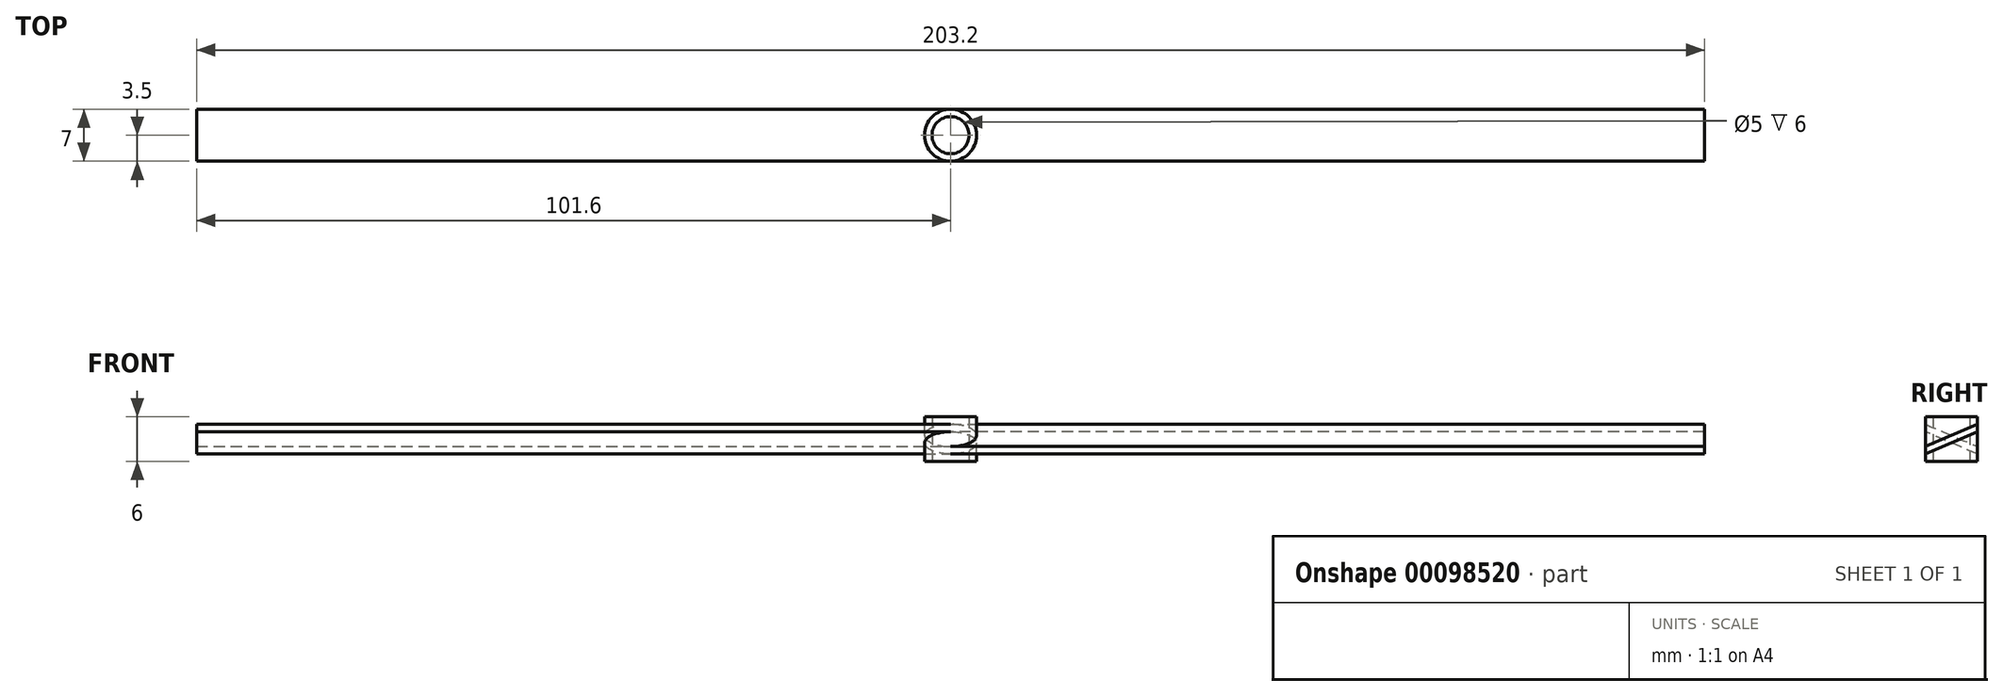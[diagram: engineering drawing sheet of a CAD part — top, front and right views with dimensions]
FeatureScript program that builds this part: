
annotation { "Feature Type Name" : "Feature", "Feature Type Description" : "" }
export const myFeature = defineFeature(function(context is Context, id is Id, definition is map)
    precondition{}
    {
        {
            var Q0;
            Q0=qCreatedBy(makeId("Top.planeOp"),FACE);
            var sketch = newSketch(context, id + "F0", { "sketchPlane" : qUnion([Q0])});
            skCircle(sketch, "E0", {"center": v(0, 0) * mm, "radius": 2.5 * mm});
            skLineSegment(sketch, "E1", {"start": v(0, 0) * mm, "end": v(2.5, 0) * mm});
            skLineSegment(sketch, "E2", {"start": v(0, 0) * mm, "end": v(101.6, 0) * mm});
            skLineSegment(sketch, "E3", {"start": v(0, 0) * mm, "end": v(-101.6, 0) * mm});
            skCircle(sketch, "E4", {"center": v(0, 0) * mm, "radius": 3.5 * mm});
            skLineSegment(sketch, "E5", {"start": v(0, 0) * mm, "end": v(0, 3.5) * mm});
            skLineSegment(sketch, "E6", {"start": v(0, 3.5) * mm, "end": v(0, -3.5) * mm});
            skLineSegment(sketch, "E7", {"start": v(0, 3.5) * mm, "end": v(-101.6, 3.5) * mm});
            skLineSegment(sketch, "E8", {"start": v(0, -3.5) * mm, "end": v(-101.6, -3.5) * mm});
            skLineSegment(sketch, "E9", {"start": v(-101.6, -3.5) * mm, "end": v(-101.6, 3.5) * mm});
            skLineSegment(sketch, "E10", {"start": v(0, 3.5) * mm, "end": v(101.6, 3.5) * mm});
            skLineSegment(sketch, "E11", {"start": v(0, -3.5) * mm, "end": v(101.6, -3.5) * mm});
            skLineSegment(sketch, "E12", {"start": v(101.6, -3.5) * mm, "end": v(101.6, 3.5) * mm});
            skSolve(sketch);
        }
        {
            var Q0;
            Q0 = qSketchRegion(id + "F0", true);
            extrude(context, id + "F1", {"entities" : qUnion([Q0]), "depth" : 4 * mm});
        }
        {
            var Q0;
            Q0=makeQuery(id+"F1.opExtrude","CAP_FACE",FACE,{"disambiguationData":[OSD([sQuery(id+"F0.wireOp",EDGE,"E0"),sQuery(id+"F0.wireOp",EDGE,"E7"),sQuery(id+"F0.wireOp",EDGE,"E8"),sQuery(id+"F0.wireOp",EDGE,"E9"),sQuery(id+"F0.wireOp",EDGE,"E10"),sQuery(id+"F0.wireOp",EDGE,"E11"),sQuery(id+"F0.wireOp",EDGE,"E12")])],"isStart":false});
            var sketch = newSketch(context, id + "F2", { "sketchPlane" : qUnion([Q0])});
            skCircle(sketch, "E13", {"center": v(0, 0) * mm, "radius": 3.5 * mm});
            skLineSegment(sketch, "E14", {"start": v(0, 0) * mm, "end": v(3.5, 0) * mm});
            skLineSegment(sketch, "E15", {"start": v(3.5, 0) * mm, "end": v(-3.5, 0) * mm});
            skLineSegment(sketch, "E16", {"start": v(-3.5, 0) * mm, "end": v(-3.5, 3.5) * mm});
            skLineSegment(sketch, "E17", {"start": v(-3.5, 3.5) * mm, "end": v(-3.5, -3.5) * mm});
            skLineSegment(sketch, "E18", {"start": v(3.5, 0) * mm, "end": v(3.5, 3.5) * mm});
            skLineSegment(sketch, "E19", {"start": v(3.5, 3.5) * mm, "end": v(3.5, -3.5) * mm});
            skSolve(sketch);
        }
        {
            var Q0;
            {var subQ0=sQuery(id+"F2.wireOp",EDGE,"E17");var subQ1=sQuery(id+"F2.wireOp",EDGE,"E13");var subQ2=makeQuery(id+"F2.imprint","INTERSECT",VERTEX,{"derivedFrom":[subQ1,sQuery(id+"F2.wireOp",EDGE,"E15"),subQ0]});Q0=makeQuery(id+"F2.imprint","IMPRINT",FACE,{"disambiguationData":[TD([[makeQuery(id+"F2.imprint","IMPRINT",EDGE,{"disambiguationData":[TD([[subQ2,1.0]])],"derivedFrom":subQ1}),-1.0]])]});}
            var Q1;
            {var subQ0=sQuery(id+"F2.wireOp",EDGE,"E19");var subQ1=sQuery(id+"F2.wireOp",EDGE,"E13");var subQ2=makeQuery(id+"F2.imprint","INTERSECT",VERTEX,{"derivedFrom":[subQ1,sQuery(id+"F2.wireOp",EDGE,"E15"),subQ0]});Q1=makeQuery(id+"F2.imprint","IMPRINT",FACE,{"disambiguationData":[TD([[makeQuery(id+"F2.imprint","IMPRINT",EDGE,{"disambiguationData":[TD([[subQ2,-1.0]])],"derivedFrom":subQ1}),-1.0]])]});}
            var Q2;
            {var subQ0=sQuery(id+"F2.wireOp",EDGE,"E19");var subQ1=sQuery(id+"F2.wireOp",EDGE,"E13");var subQ2=makeQuery(id+"F2.imprint","INTERSECT",VERTEX,{"derivedFrom":[subQ1,sQuery(id+"F2.wireOp",EDGE,"E15"),subQ0]});Q2=makeQuery(id+"F2.imprint","IMPRINT",FACE,{"disambiguationData":[TD([[makeQuery(id+"F2.imprint","IMPRINT",EDGE,{"disambiguationData":[TD([[subQ2,1.0]])],"derivedFrom":subQ1}),-1.0]])]});}
            var Q3;
            {var subQ0=sQuery(id+"F2.wireOp",EDGE,"E17");var subQ1=sQuery(id+"F2.wireOp",EDGE,"E13");var subQ2=makeQuery(id+"F2.imprint","INTERSECT",VERTEX,{"derivedFrom":[subQ1,sQuery(id+"F2.wireOp",EDGE,"E15"),subQ0]});Q3=makeQuery(id+"F2.imprint","IMPRINT",FACE,{"disambiguationData":[TD([[makeQuery(id+"F2.imprint","IMPRINT",EDGE,{"disambiguationData":[TD([[subQ2,-1.0]])],"derivedFrom":subQ1}),-1.0]])]});}
            var Q4;
            {var subQ0=sQuery(id+"F2.wireOp",EDGE,"E15");var subQ3=makeQuery(id+"F1.opExtrude","CAP_EDGE",EDGE,{"disambiguationData":[OSD([sQuery(id+"F0.wireOp",EDGE,"E0")])],"isStart":false});var subQ6=makeQuery(id+"F2.imprint","INTERSECT",VERTEX,{"disambiguationData":[OD(0.0)],"derivedFrom":[subQ3,subQ0]});Q4=makeQuery(id+"F2.imprint","IMPRINT",FACE,{"disambiguationData":[TD([[makeQuery(id+"F2.imprint","IMPRINT",EDGE,{"disambiguationData":[TD([[subQ6,-1.0]])],"derivedFrom":subQ3}),-1.0]])]});}
            var Q5;
            {var subQ0=sQuery(id+"F2.wireOp",EDGE,"E15");var subQ3=makeQuery(id+"F1.opExtrude","CAP_EDGE",EDGE,{"disambiguationData":[OSD([sQuery(id+"F0.wireOp",EDGE,"E0")])],"isStart":false});var subQ5=makeQuery(id+"F2.imprint","INTERSECT",VERTEX,{"disambiguationData":[OD(0.0)],"derivedFrom":[subQ3,subQ0]});Q5=makeQuery(id+"F2.imprint","IMPRINT",FACE,{"disambiguationData":[TD([[makeQuery(id+"F2.imprint","IMPRINT",EDGE,{"disambiguationData":[TD([[subQ5,1.0]])],"derivedFrom":subQ3}),-1.0]])]});}
            extrude(context, id + "F3", {"entities" : qUnion([Q0, Q1, Q2, Q3, Q4, Q5]), "operationType" : NewBodyOperationType.ADD, "depth" : 1 * mm});
        }
        {
            var Q0;
            {var subQ0=sQuery(id+"F0.wireOp",EDGE,"E12");var subQ1=sQuery(id+"F0.wireOp",EDGE,"E11");var subQ2=sQuery(id+"F0.wireOp",EDGE,"E8");Q0=makeQuery(id+"F3.boolean.opBoolean","SPLIT",EDGE,{"disambiguationData":[TD([makeQuery(id+"F1.opExtrude","SWEPT_FACE",FACE,{"disambiguationData":[OSD([subQ0])]})])],"derivedFrom":makeQuery(id+"F1.opExtrude","CAP_EDGE",EDGE,{"disambiguationData":[OSD([subQ2,subQ1])],"isStart":false})});}
            chamfer(context, id + "F4", {"entities" : qUnion([Q0]), "chamferType" : ChamferType.TWO_OFFSETS, "width1" : 7 * mm, "oppositeDirection" : false, "width2" : 3 * mm, "tangentPropagation" : true});
        }
        {
            var Q0;
            {var subQ0=sQuery(id+"F0.wireOp",EDGE,"E9");var subQ1=sQuery(id+"F0.wireOp",EDGE,"E10");var subQ2=sQuery(id+"F0.wireOp",EDGE,"E7");Q0=makeQuery(id+"F3.boolean.opBoolean","SPLIT",EDGE,{"disambiguationData":[TD([makeQuery(id+"F1.opExtrude","SWEPT_FACE",FACE,{"disambiguationData":[OSD([subQ0])]})])],"derivedFrom":makeQuery(id+"F1.opExtrude","CAP_EDGE",EDGE,{"disambiguationData":[OSD([subQ2,subQ1])],"isStart":false})});}
            chamfer(context, id + "F5", {"entities" : qUnion([Q0]), "chamferType" : ChamferType.TWO_OFFSETS, "width1" : 3 * mm, "oppositeDirection" : false, "width2" : 7 * mm, "tangentPropagation" : true});
        }
        {
            var Q0;
            Q0=makeQuery(id+"F1.opExtrude","CAP_FACE",FACE,{"disambiguationData":[OSD([sQuery(id+"F0.wireOp",EDGE,"E0"),sQuery(id+"F0.wireOp",EDGE,"E7"),sQuery(id+"F0.wireOp",EDGE,"E8"),sQuery(id+"F0.wireOp",EDGE,"E9"),sQuery(id+"F0.wireOp",EDGE,"E10"),sQuery(id+"F0.wireOp",EDGE,"E11"),sQuery(id+"F0.wireOp",EDGE,"E12")])],"isStart":true});
            var sketch = newSketch(context, id + "F6", { "sketchPlane" : qUnion([Q0])});
            skCircle(sketch, "E20.cCircle", {"center": v(0, 0) * mm, "radius": 3.5 * mm, "construction": true});
            skLineSegment(sketch, "E20.0", {"start": v(3.5, -3.5) * mm, "end": v(-3.5, -3.5) * mm});
            skLineSegment(sketch, "E20.1", {"start": v(-3.5, -3.5) * mm, "end": v(-3.5, 3.5) * mm});
            skLineSegment(sketch, "E20.2", {"start": v(-3.5, 3.5) * mm, "end": v(3.5, 3.5) * mm});
            skLineSegment(sketch, "E20.3", {"start": v(3.5, 3.5) * mm, "end": v(3.5, -3.5) * mm});
            skPoint(sketch, "E20.0.midPoint", {"position": v(0, -3.5) * mm});
            skSolve(sketch);
        }
        {
            var Q0;
            Q0=makeQuery(id+"F6.imprint","IMPRINT",FACE,{"disambiguationData":[TD([[makeQuery(id+"F6.imprint","IMPRINT",EDGE,{"derivedFrom":sQuery(id+"F6.wireOp",EDGE,"E20.0")}),1.0]])]});
            extrude(context, id + "F7", {"entities" : qUnion([Q0]), "operationType" : NewBodyOperationType.ADD, "depth" : 1 * mm});
        }
        {
            var Q0;
            {var subQ0=sQuery(id+"F0.wireOp",EDGE,"E10");var subQ1=sQuery(id+"F0.wireOp",EDGE,"E7");var subQ2=sQuery(id+"F0.wireOp",EDGE,"E12");Q0=makeQuery(id+"F7.boolean.opBoolean","SPLIT",EDGE,{"disambiguationData":[TD([makeQuery(id+"F1.opExtrude","SWEPT_FACE",FACE,{"disambiguationData":[OSD([subQ2])]})])],"derivedFrom":makeQuery(id+"F1.opExtrude","CAP_EDGE",EDGE,{"disambiguationData":[OSD([subQ1,subQ0])],"isStart":true})});}
            chamfer(context, id + "F8", {"entities" : qUnion([Q0]), "chamferType" : ChamferType.TWO_OFFSETS, "width1" : 7 * mm, "oppositeDirection" : false, "width2" : 3 * mm, "tangentPropagation" : true});
        }
        {
            var Q0;
            {var subQ0=sQuery(id+"F0.wireOp",EDGE,"E11");var subQ1=sQuery(id+"F0.wireOp",EDGE,"E8");var subQ2=sQuery(id+"F0.wireOp",EDGE,"E9");Q0=makeQuery(id+"F7.boolean.opBoolean","SPLIT",EDGE,{"disambiguationData":[TD([makeQuery(id+"F1.opExtrude","SWEPT_FACE",FACE,{"disambiguationData":[OSD([subQ2])]})])],"derivedFrom":makeQuery(id+"F1.opExtrude","CAP_EDGE",EDGE,{"disambiguationData":[OSD([subQ1,subQ0])],"isStart":true})});}
            chamfer(context, id + "F9", {"entities" : qUnion([Q0]), "chamferType" : ChamferType.TWO_OFFSETS, "width1" : 3 * mm, "oppositeDirection" : false, "width2" : 7 * mm, "tangentPropagation" : true});
        }
        {
            var Q0;
            Q0=makeQuery(id+"F7.opExtrude","SWEPT_EDGE",EDGE,{"disambiguationData":[OSD([sQuery(id+"F0.wireOp",EDGE,"E8"),sQuery(id+"F0.wireOp",EDGE,"E11"),sQuery(id+"F6.wireOp",EDGE,"E20.2"),sQuery(id+"F6.wireOp",EDGE,"E20.3")])]});
            var Q1;
            Q1=makeQuery(id+"F7.opExtrude","SWEPT_EDGE",EDGE,{"disambiguationData":[OSD([sQuery(id+"F0.wireOp",EDGE,"E8"),sQuery(id+"F0.wireOp",EDGE,"E11"),sQuery(id+"F6.wireOp",EDGE,"E20.1"),sQuery(id+"F6.wireOp",EDGE,"E20.2")])]});
            var Q2;
            Q2=makeQuery(id+"F3.opExtrude","SWEPT_EDGE",EDGE,{"disambiguationData":[OSD([sQuery(id+"F0.wireOp",EDGE,"E8"),sQuery(id+"F0.wireOp",EDGE,"E11"),sQuery(id+"F2.wireOp",EDGE,"E17")])]});
            var Q3;
            Q3=makeQuery(id+"F3.opExtrude","SWEPT_EDGE",EDGE,{"disambiguationData":[OSD([sQuery(id+"F0.wireOp",EDGE,"E8"),sQuery(id+"F0.wireOp",EDGE,"E11"),sQuery(id+"F2.wireOp",EDGE,"E19")])]});
            var Q4;
            Q4=makeQuery(id+"F7.opExtrude","SWEPT_EDGE",EDGE,{"disambiguationData":[OSD([sQuery(id+"F0.wireOp",EDGE,"E7"),sQuery(id+"F0.wireOp",EDGE,"E10"),sQuery(id+"F6.wireOp",EDGE,"E20.0"),sQuery(id+"F6.wireOp",EDGE,"E20.3")])]});
            var Q5;
            Q5=makeQuery(id+"F3.opExtrude","SWEPT_EDGE",EDGE,{"disambiguationData":[OSD([sQuery(id+"F0.wireOp",EDGE,"E7"),sQuery(id+"F0.wireOp",EDGE,"E10"),sQuery(id+"F2.wireOp",EDGE,"E19")])]});
            var Q6;
            Q6=makeQuery(id+"F3.opExtrude","SWEPT_EDGE",EDGE,{"disambiguationData":[OSD([sQuery(id+"F0.wireOp",EDGE,"E7"),sQuery(id+"F0.wireOp",EDGE,"E10"),sQuery(id+"F2.wireOp",EDGE,"E17")])]});
            var Q7;
            Q7=makeQuery(id+"F7.opExtrude","SWEPT_EDGE",EDGE,{"disambiguationData":[OSD([sQuery(id+"F0.wireOp",EDGE,"E7"),sQuery(id+"F0.wireOp",EDGE,"E10"),sQuery(id+"F6.wireOp",EDGE,"E20.0"),sQuery(id+"F6.wireOp",EDGE,"E20.1")])]});
            fillet(context, id + "F10", {"entities" : qUnion([Q0, Q1, Q2, Q3, Q4, Q5, Q6, Q7]), "radius" : 3.5 * mm, "tangentPropagation" : true, "allowEdgeOverflow" : false});
        }
    });
